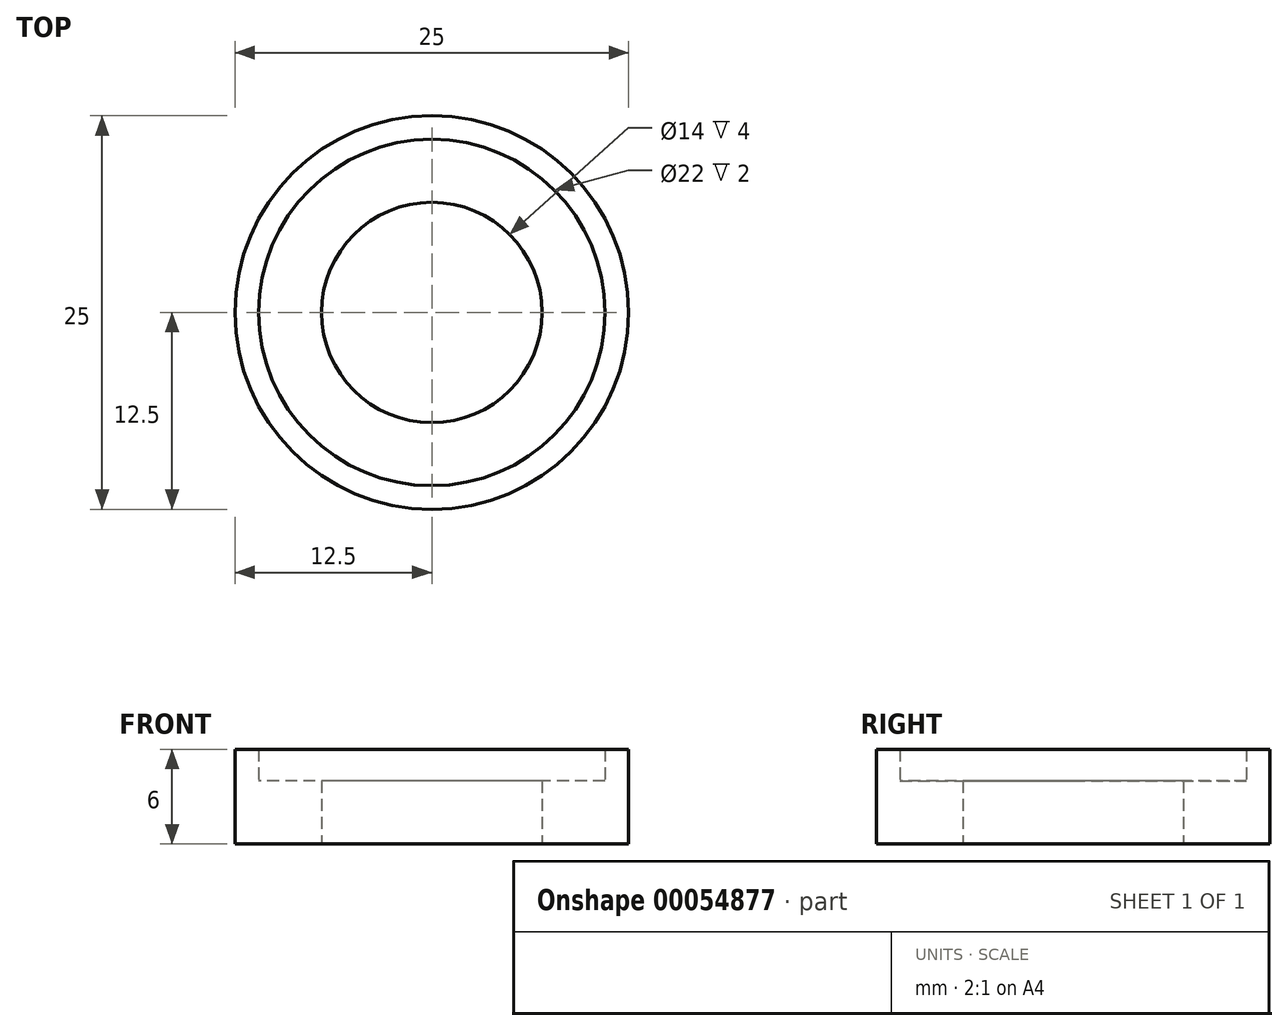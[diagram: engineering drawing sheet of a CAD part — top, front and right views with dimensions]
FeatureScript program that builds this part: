
annotation { "Feature Type Name" : "Feature", "Feature Type Description" : "" }
export const myFeature = defineFeature(function(context is Context, id is Id, definition is map)
    precondition{}
    {
        {
            var Q0;
            Q0=qCreatedBy(makeId("Top.planeOp"),FACE);
            var sketch = newSketch(context, id + "F0", { "sketchPlane" : qUnion([Q0])});
            skCircle(sketch, "E0", {"center": v(0, 0) * mm, "radius": 7 * mm});
            skCircle(sketch, "E1", {"center": v(0, 0) * mm, "radius": 12.5 * mm});
            skSolve(sketch);
        }
        {
            var Q0;
            Q0 = qSketchRegion(id + "F0", true);
            extrude(context, id + "F1", {"entities" : qUnion([Q0]), "depth" : 4 * mm});
        }
        {
            var Q0;
            Q0=makeQuery(id+"F1.opExtrude","CAP_FACE",FACE,{"disambiguationData":[OSD([sQuery(id+"F0.wireOp",EDGE,"E0"),sQuery(id+"F0.wireOp",EDGE,"E1")])],"isStart":false});
            var sketch = newSketch(context, id + "F2", { "sketchPlane" : qUnion([Q0])});
            skCircle(sketch, "E2", {"center": v(0, 0) * mm, "radius": 11 * mm});
            skCircle(sketch, "E3", {"center": v(0, 0) * mm, "radius": 12.5 * mm});
            skSolve(sketch);
        }
        {
            var Q0;
            Q0=makeQuery(id+"F2.imprint","IMPRINT",FACE,{"disambiguationData":[TD([[makeQuery(id+"F2.imprint","IMPRINT",EDGE,{"derivedFrom":sQuery(id+"F2.wireOp",EDGE,"E2")}),-1.0]])]});
            extrude(context, id + "F3", {"entities" : qUnion([Q0]), "operationType" : NewBodyOperationType.ADD, "depth" : 2 * mm});
        }
    });
